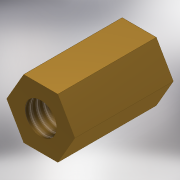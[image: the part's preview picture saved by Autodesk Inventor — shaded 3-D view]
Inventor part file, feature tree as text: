
AUTODESK INVENTOR PART (.ipt)
format: ipt  version: 2018.2 (Build 222227000, 227)  size: 113,152 bytes
history: native  units: mm
features: sketch x2, extrude x1, hole x1
ambient origin geometry x8: Origin, YZ Plane, XZ Plane, XY Plane, X Axis, Y Axis, Z Axis, Center Point
bodies: Solid1 (feature_tree)
feature tree (4):
  extrude  "Extrusion1"  Depth=10.0mm TaperAngle=0.0deg
  hole  "Hole1"  [1 undecoded]
  sketch  "Sketch1"  dims[d0=3.0mm d1=10.0mm d2=0.0mm]
  sketch  "Sketch2"  dims[d3=3.242mm d4=8.0mm d5=4.0mm d6=2.0mm d7=90.0deg d8=8.0mm d9=20.594885mm]
note: 1 required parameter value undecoded (feature->parameter linkage not recoverable at this tier; creation-order binding heuristic only, values carry confidence <= 0.55)
